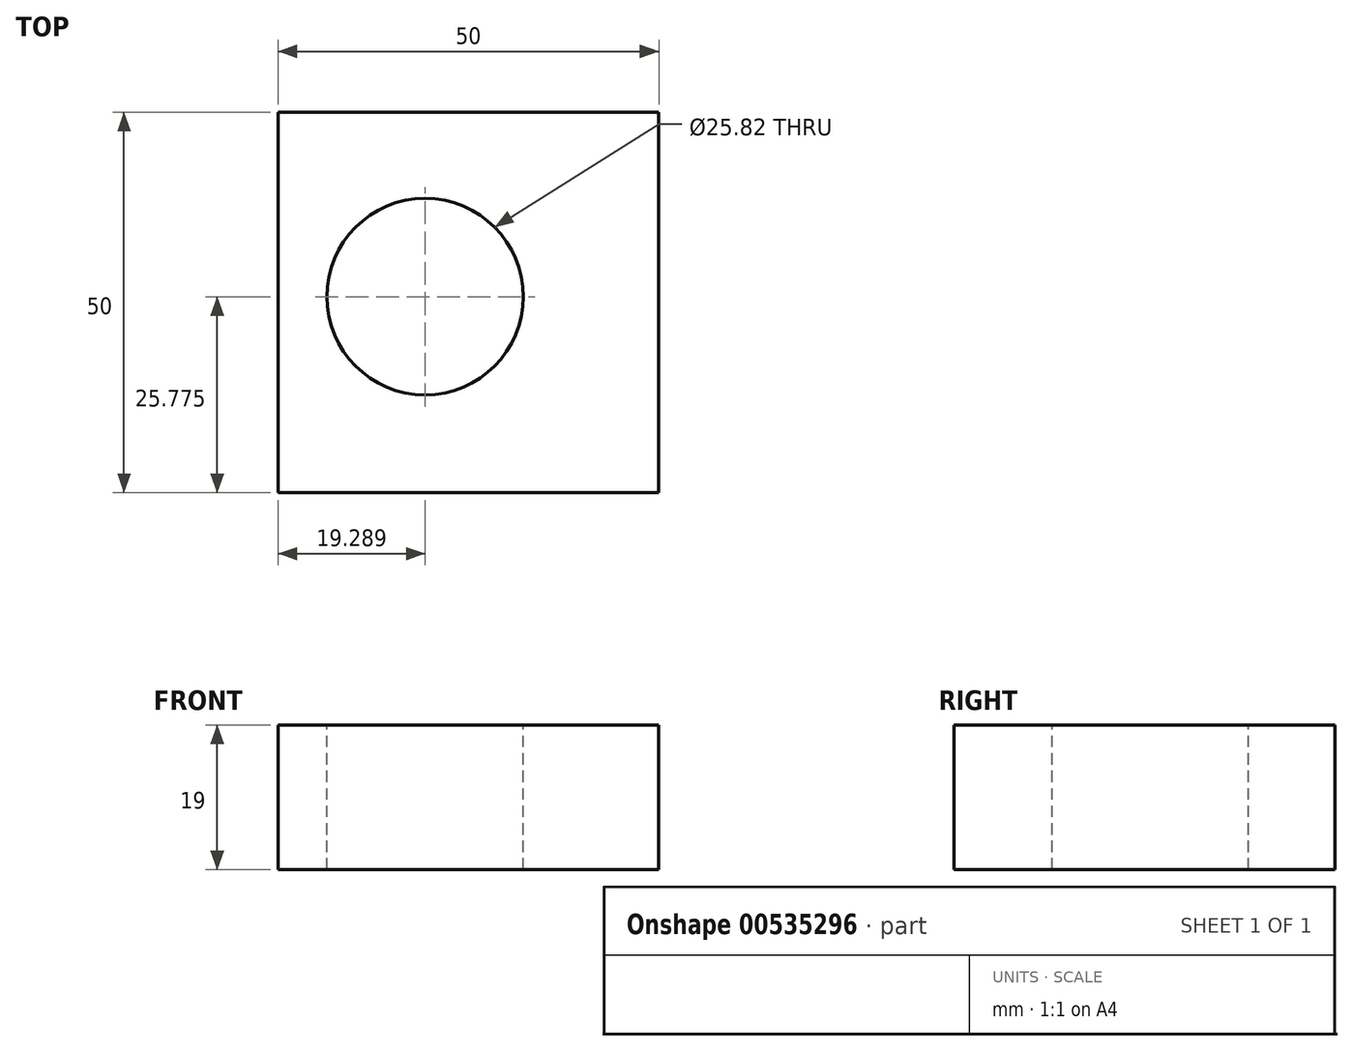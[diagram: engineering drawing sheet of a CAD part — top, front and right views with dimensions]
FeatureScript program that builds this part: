
annotation { "Feature Type Name" : "Feature", "Feature Type Description" : "" }
export const myFeature = defineFeature(function(context is Context, id is Id, definition is map)
    precondition{}
    {
        {
            var Q0;
            Q0=qCreatedBy(makeId("Top.planeOp"),FACE);
            var sketch = newSketch(context, id + "F0", { "sketchPlane" : qUnion([Q0])});
            skPoint(sketch, "E0.oppositeSnap0", {"position": v(-7.18, 40.53) * mm});
            skLineSegment(sketch, "E1.bottom", {"start": v(0.72, 5.72) * mm, "end": v(50.72, 5.72) * mm});
            skLineSegment(sketch, "E1.top", {"start": v(0.72, -44.28) * mm, "end": v(50.72, -44.28) * mm});
            skLineSegment(sketch, "E1.left", {"start": v(0.72, 5.72) * mm, "end": v(0.72, -44.28) * mm});
            skLineSegment(sketch, "E1.right", {"start": v(50.72, 5.72) * mm, "end": v(50.72, -44.28) * mm});
            skSolve(sketch);
        }
        {
            var Q0;
            Q0 = qSketchRegion(id + "F0", true);
            extrude(context, id + "F1", {"entities" : qUnion([Q0]), "depth" : 19 * mm, "offsetDistance" : 25 * mm});
        }
        {
            var Q0;
            Q0=makeQuery(id+"F1.opExtrude","CAP_FACE",FACE,{"disambiguationData":[OSD([sQuery(id+"F0.wireOp",EDGE,"E1.bottom"),sQuery(id+"F0.wireOp",EDGE,"E1.top"),sQuery(id+"F0.wireOp",EDGE,"E1.left"),sQuery(id+"F0.wireOp",EDGE,"E1.right")])],"isStart":false});
            var sketch = newSketch(context, id + "F2", { "sketchPlane" : qUnion([Q0])});
            skCircle(sketch, "E2", {"center": v(20, -18.5) * mm, "radius": 12.9 * mm});
            skSolve(sketch);
        }
        {
            var Q0;
            Q0 = qSketchRegion(id + "F2", true);
            extrude(context, id + "F3", {"entities" : qUnion([Q0]), "operationType" : NewBodyOperationType.REMOVE, "endBound" : BoundingType.UP_TO_NEXT, "oppositeDirection" : true, "depth" : 19 * mm, "offsetDistance" : 25 * mm});
        }
    });
